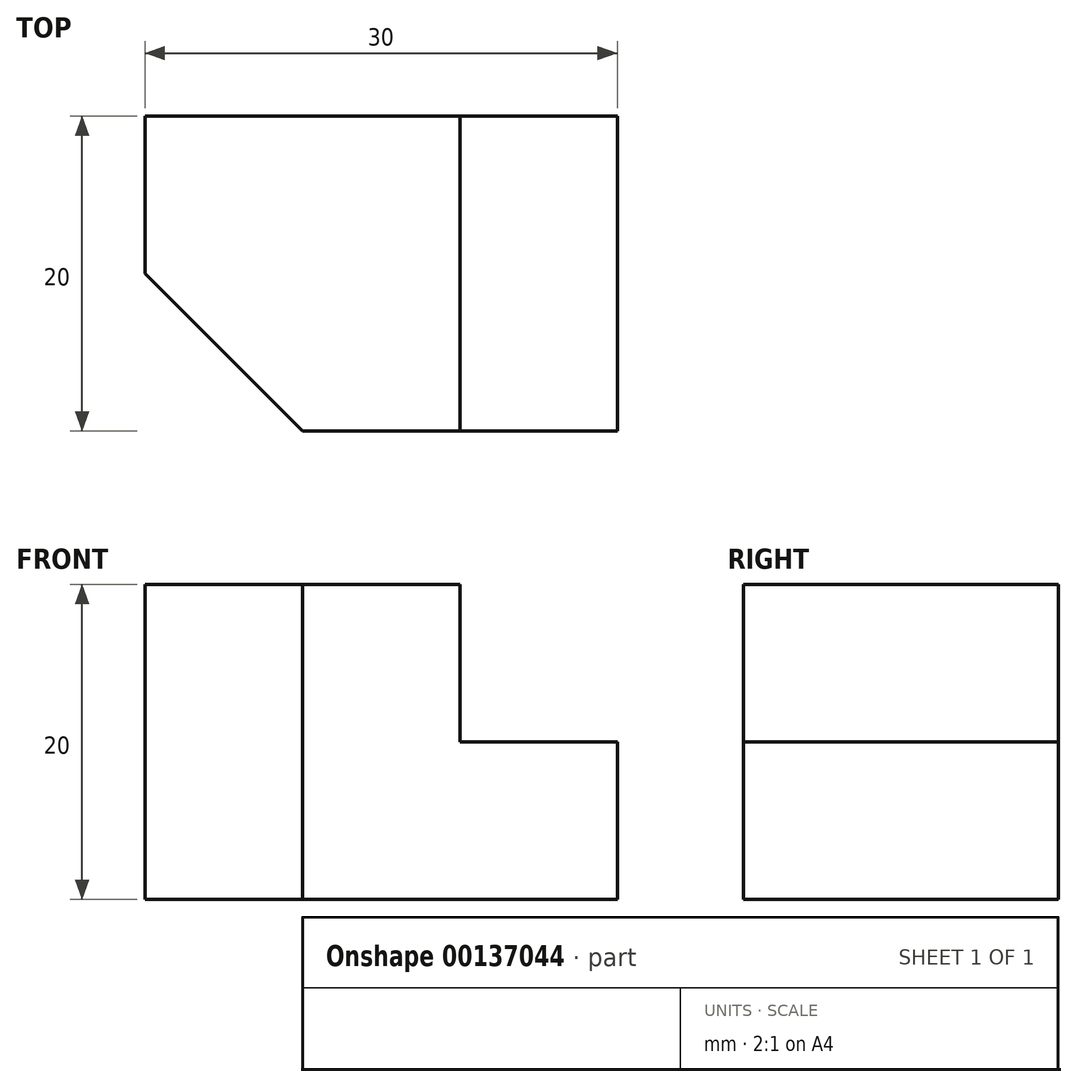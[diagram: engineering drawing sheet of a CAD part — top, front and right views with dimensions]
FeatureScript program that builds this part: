
annotation { "Feature Type Name" : "Feature", "Feature Type Description" : "" }
export const myFeature = defineFeature(function(context is Context, id is Id, definition is map)
    precondition{}
    {
        {
            var Q0;
            Q0=qCreatedBy(makeId("Front.planeOp"),FACE);
            var sketch = newSketch(context, id + "F0", { "sketchPlane" : qUnion([Q0])});
            skLineSegment(sketch, "E0", {"start": v(0, 0) * mm, "end": v(0, 20) * mm});
            skLineSegment(sketch, "E1", {"start": v(0, 20) * mm, "end": v(10, 20) * mm});
            skLineSegment(sketch, "E2", {"start": v(10, 20) * mm, "end": v(10, 0) * mm});
            skLineSegment(sketch, "E3", {"start": v(10, 0) * mm, "end": v(0, 0) * mm});
            skLineSegment(sketch, "E4", {"start": v(10, 20) * mm, "end": v(20, 20) * mm});
            skLineSegment(sketch, "E5", {"start": v(20, 20) * mm, "end": v(20, 10) * mm});
            skLineSegment(sketch, "E6", {"start": v(20, 10) * mm, "end": v(30, 10) * mm});
            skLineSegment(sketch, "E7", {"start": v(30, 10) * mm, "end": v(30, 0) * mm});
            skLineSegment(sketch, "E8", {"start": v(30, 0) * mm, "end": v(10, 0) * mm});
            skSolve(sketch);
        }
        {
            var Q0;
            Q0=makeQuery(id+"F0.imprint","IMPRINT",FACE,{"disambiguationData":[TD([[makeQuery(id+"F0.imprint","IMPRINT",EDGE,{"derivedFrom":sQuery(id+"F0.wireOp",EDGE,"E0")}),-1.0]])]});
            var Q1;
            Q1=makeQuery(id+"F0.imprint","IMPRINT",FACE,{"disambiguationData":[TD([[makeQuery(id+"F0.imprint","IMPRINT",EDGE,{"derivedFrom":sQuery(id+"F0.wireOp",EDGE,"E2")}),1.0]])]});
            extrude(context, id + "F1", {"entities" : qUnion([Q0, Q1]), "depth" : 20 * mm});
        }
        {
            var Q0;
            Q0=qCreatedBy(makeId("Top.planeOp"),FACE);
            var sketch = newSketch(context, id + "F2", { "sketchPlane" : qUnion([Q0])});
            skLineSegment(sketch, "E9.bottom", {"start": v(0, 0) * mm, "end": v(20, 0) * mm});
            skLineSegment(sketch, "E9.right", {"start": v(20, 0) * mm, "end": v(20, -20) * mm});
            skLineSegment(sketch, "E10", {"start": v(0, 0) * mm, "end": v(0, -20) * mm});
            skLineSegment(sketch, "E11", {"start": v(0, -20) * mm, "end": v(20, -20) * mm});
            skLineSegment(sketch, "E12", {"start": v(0, -10) * mm, "end": v(10, -20) * mm});
            skLineSegment(sketch, "E13", {"start": v(0, -20) * mm, "end": v(10, -20) * mm});
            skLineSegment(sketch, "E14", {"start": v(0, -20) * mm, "end": v(0, -10) * mm});
            skSolve(sketch);
        }
        {
            var Q0;
            Q0=makeQuery(id+"F2.imprint","IMPRINT",FACE,{"disambiguationData":[TD([[makeQuery(id+"F2.imprint","IMPRINT",EDGE,{"derivedFrom":sQuery(id+"F2.wireOp",EDGE,"E12")}),-1.0]])]});
            var Q1;
            Q1=sQuery(id+"F2.wireOp",EDGE,"E12");
            var Q2;
            Q2=sQuery(id+"F2.wireOp",EDGE,"E13");
            var Q3;
            Q3=sQuery(id+"F2.wireOp",EDGE,"E14");
            extrude(context, id + "F3", {"entities" : qUnion([Q0]), "operationType" : NewBodyOperationType.REMOVE, "surfaceEntities" : qUnion([Q1, Q2, Q3]), "endBound" : BoundingType.THROUGH_ALL, "depth" : 25 * mm});
        }
    });
